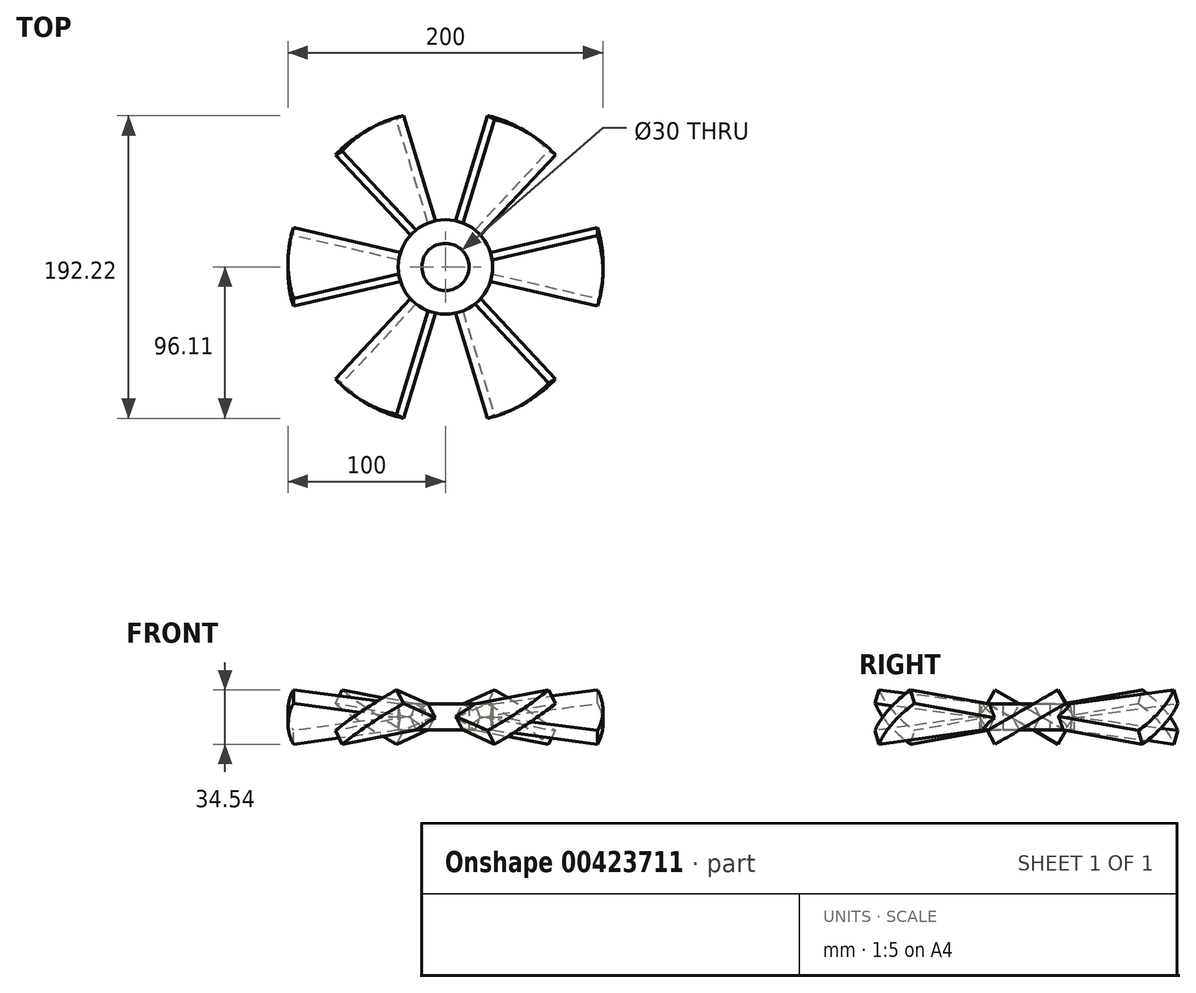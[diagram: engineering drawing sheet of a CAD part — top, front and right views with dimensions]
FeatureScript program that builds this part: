
annotation { "Feature Type Name" : "Feature", "Feature Type Description" : "" }
export const myFeature = defineFeature(function(context is Context, id is Id, definition is map)
    precondition{}
    {
        {
            var Q0;
            Q0=qCreatedBy(makeId("Top.planeOp"),FACE);
            var sketch = newSketch(context, id + "F0", { "sketchPlane" : qUnion([Q0])});
            skLineSegment(sketch, "E0", {"start": v(0, 0) * mm, "end": v(79.06, 0) * mm});
            skSolve(sketch);
        }
        {
            var Q0;
            Q0=sQuery(id+"F0.wireOp",EDGE,"E0");
            cPlane(context, id + "F1", {"entities" : qUnion([Q0]), "cplaneType" : CPlaneType.LINE_ANGLE, "offset" : 25 * mm, "angle" : 60 * degree, "oppositeDirection" : true, "width" : 150 * mm, "height" : 150 * mm});
        }
        {
            var Q0;
            Q0=qCreatedBy(id+"F1.planeOp",FACE);
            var sketch = newSketch(context, id + "F2", { "sketchPlane" : qUnion([Q0])});
            skArc(sketch, "E1", {"start": v(24.15, -6.47) * mm, "mid": v(24.79, -3.26) * mm, "end": v(25, 0) * mm});
            skLineSegment(sketch, "E2", {"start": v(0, 0) * mm, "end": v(170.42, 0) * mm, "construction": true});
            skArc(sketch, "E3", {"start": v(96.6, -25.88) * mm, "mid": v(99.14, -13.05) * mm, "end": v(100, 0) * mm});
            skLineSegment(sketch, "E4", {"start": v(24.15, -6.47) * mm, "end": v(96.6, -25.88) * mm});
            skArc(sketch, "E5.MirrorCS", {"start": v(96.6, 25.88) * mm, "mid": v(99.14, 13.05) * mm, "end": v(100, 0) * mm});
            skLineSegment(sketch, "E6.MirrorCS", {"start": v(24.15, 6.47) * mm, "end": v(96.6, 25.88) * mm});
            skArc(sketch, "E7.MirrorCS", {"start": v(24.15, 6.47) * mm, "mid": v(24.79, 3.26) * mm, "end": v(25, 0) * mm});
            skSolve(sketch);
        }
        {
            var Q0;
            Q0=makeQuery(id+"F2.imprint","IMPRINT",FACE,{"disambiguationData":[TD([[makeQuery(id+"F2.imprint","IMPRINT",EDGE,{"derivedFrom":sQuery(id+"F2.wireOp",EDGE,"E1")}),-1.0]])]});
            extrude(context, id + "F3", {"entities" : qUnion([Q0]), "depth" : 5 * mm, "hasSecondDirection" : true, "secondDirectionOppositeDirection" : true, "secondDirectionDepth" : 5 * mm});
        }
        {
            var Q0;
            Q0=qCreatedBy(makeId("Front.planeOp"),FACE);
            var sketch = newSketch(context, id + "F4", { "sketchPlane" : qUnion([Q0])});
            skLineSegment(sketch, "E8", {"start": v(0, 32.6) * mm, "end": v(0, -40.7) * mm, "construction": true});
            skSolve(sketch);
        }
        {
            var Q0;
            Q0=makeQuery(id+"F3.opExtrude","SWEPT_BODY",BODY,{"disambiguationData":[OSD([sQuery(id+"F2.wireOp",EDGE,"E1"),sQuery(id+"F2.wireOp",EDGE,"E3"),sQuery(id+"F2.wireOp",EDGE,"E4"),sQuery(id+"F2.wireOp",EDGE,"E5.MirrorCS"),sQuery(id+"F2.wireOp",EDGE,"E6.MirrorCS"),sQuery(id+"F2.wireOp",EDGE,"E7.MirrorCS")])]});
            var Q1;
            Q1=sQuery(id+"F4.wireOp",EDGE,"E8");
            circularPattern(context, id + "F5", {"entities" : qUnion([Q0]), "axis" : qUnion([Q1]), "angle" : 360 * degree, "instanceCount" : 6, "equalSpace" : true});
        }
        {
            var Q0;
            Q0=qCreatedBy(makeId("Top.planeOp"),FACE);
            var sketch = newSketch(context, id + "F6", { "sketchPlane" : qUnion([Q0])});
            skCircle(sketch, "E9", {"center": v(0, 0) * mm, "radius": 15 * mm});
            skCircle(sketch, "E10", {"center": v(0, 0) * mm, "radius": 30 * mm});
            skPoint(sketch, "E11.0", {"position": v(24.15, 3.1) * mm});
            skSolve(sketch);
        }
        {
            var Q0;
            Q0 = qSketchRegion(id + "F6", true);
            var Q1;
            Q1=makeQuery(id+"F3.opExtrude","CAP_VERTEX",VERTEX,{"disambiguationData":[OSD([sQuery(id+"F2.wireOp",EDGE,"E1"),sQuery(id+"F2.wireOp",EDGE,"E4")])],"isStart":true});
            var Q2;
            Q2=makeQuery(id+"F3.opExtrude","CAP_VERTEX",VERTEX,{"disambiguationData":[OSD([sQuery(id+"F2.wireOp",EDGE,"E6.MirrorCS"),sQuery(id+"F2.wireOp",EDGE,"E7.MirrorCS")])],"isStart":false});
            extrude(context, id + "F7", {"entities" : qUnion([Q0]), "operationType" : NewBodyOperationType.REMOVE, "endBoundEntityVertex" : qUnion([Q1]), "depth" : 25 * mm, "hasSecondDirection" : true, "secondDirectionOppositeDirection" : true, "secondDirectionBoundEntityVertex" : qUnion([Q2]), "secondDirectionDepth" : 25 * mm});
        }
        {
            var Q0;
            Q0 = qSketchRegion(id + "F6", true);
            var Q1;
            {var subQ0=sQuery(id+"F2.wireOp",EDGE,"E4");Q1=makeQuery(id+"F7.boolean.opBoolean","INTERSECT",VERTEX,{"derivedFrom":[makeQuery(id+"F3.opExtrude","CAP_FACE",FACE,{"disambiguationData":[OSD([sQuery(id+"F2.wireOp",EDGE,"E1"),sQuery(id+"F2.wireOp",EDGE,"E3"),subQ0,sQuery(id+"F2.wireOp",EDGE,"E5.MirrorCS"),sQuery(id+"F2.wireOp",EDGE,"E6.MirrorCS"),sQuery(id+"F2.wireOp",EDGE,"E7.MirrorCS")])],"isStart":true}),makeQuery(id+"F3.opExtrude","SWEPT_FACE",FACE,{"disambiguationData":[OSD([subQ0])]}),makeQuery(id+"F7.opExtrude","SWEPT_FACE",FACE,{"disambiguationData":[OSD([sQuery(id+"F6.wireOp",EDGE,"E10")])]})]});}
            var Q2;
            {var subQ0=sQuery(id+"F2.wireOp",EDGE,"E6.MirrorCS");Q2=makeQuery(id+"F7.boolean.opBoolean","INTERSECT",VERTEX,{"derivedFrom":[makeQuery(id+"F3.opExtrude","CAP_FACE",FACE,{"disambiguationData":[OSD([sQuery(id+"F2.wireOp",EDGE,"E1"),sQuery(id+"F2.wireOp",EDGE,"E3"),sQuery(id+"F2.wireOp",EDGE,"E4"),sQuery(id+"F2.wireOp",EDGE,"E5.MirrorCS"),subQ0,sQuery(id+"F2.wireOp",EDGE,"E7.MirrorCS")])],"isStart":false}),makeQuery(id+"F3.opExtrude","SWEPT_FACE",FACE,{"disambiguationData":[OSD([subQ0])]}),makeQuery(id+"F7.opExtrude","SWEPT_FACE",FACE,{"disambiguationData":[OSD([sQuery(id+"F6.wireOp",EDGE,"E10")])]})]});}
            extrude(context, id + "F8", {"entities" : qUnion([Q0]), "endBound" : BoundingType.UP_TO_VERTEX, "endBoundEntityVertex" : qUnion([Q1]), "depth" : 25 * mm, "hasSecondDirection" : true, "secondDirectionBound" : SecondDirectionBoundingType.UP_TO_VERTEX, "secondDirectionOppositeDirection" : true, "secondDirectionBoundEntityVertex" : qUnion([Q2]), "secondDirectionDepth" : 25 * mm});
        }
    });
